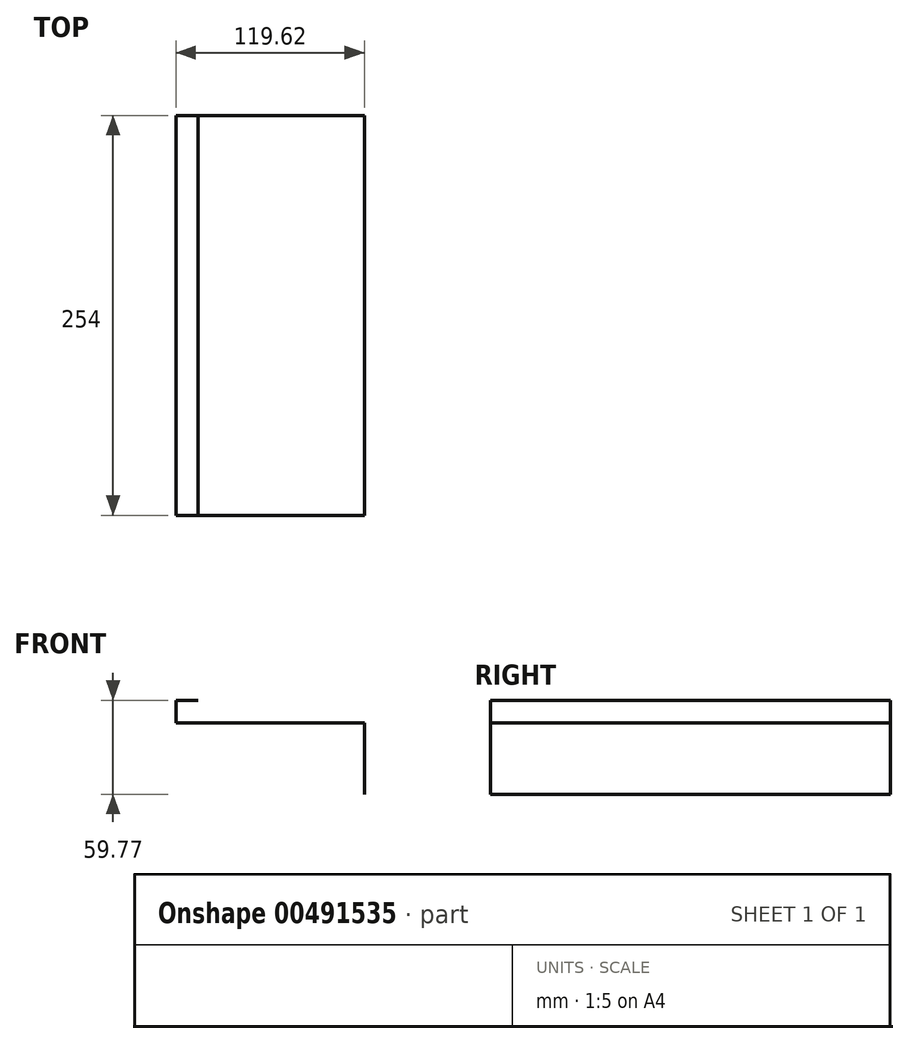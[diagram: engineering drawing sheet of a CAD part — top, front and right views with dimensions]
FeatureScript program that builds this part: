
annotation { "Feature Type Name" : "Feature", "Feature Type Description" : "" }
export const myFeature = defineFeature(function(context is Context, id is Id, definition is map)
    precondition{}
    {
        {
            var Q0;
            Q0=qCreatedBy(makeId("Front.planeOp"),FACE);
            var sketch = newSketch(context, id + "F0", { "sketchPlane" : qUnion([Q0])});
            skLineSegment(sketch, "E0", {"start": v(-47.98, 39.79) * mm, "end": v(-62.15, 39.79) * mm});
            skLineSegment(sketch, "E1", {"start": v(-62.15, 39.79) * mm, "end": v(-62.15, 25.3) * mm});
            skLineSegment(sketch, "E2", {"start": v(-62.15, 25.3) * mm, "end": v(57.47, 25.3) * mm});
            skLineSegment(sketch, "E3", {"start": v(57.47, 25.3) * mm, "end": v(57.47, -19.98) * mm});
            skSolve(sketch);
        }
        {
            var Q0;
            Q0=sQuery(id+"F0.wireOp",EDGE,"E2");
            var Q1;
            Q1=sQuery(id+"F0.wireOp",EDGE,"E3");
            var Q2;
            Q2=sQuery(id+"F0.wireOp",EDGE,"E1");
            var Q3;
            Q3=sQuery(id+"F0.wireOp",EDGE,"E0");
            extrude(context, id + "F1", {"bodyType" : ToolBodyType.SURFACE, "surfaceEntities" : qUnion([Q0, Q1, Q2, Q3]), "depth" : 254 * mm});
        }
    });
